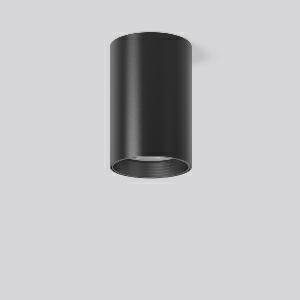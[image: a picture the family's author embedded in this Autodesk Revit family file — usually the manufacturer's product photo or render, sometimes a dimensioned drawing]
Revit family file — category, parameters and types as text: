
# Revit family: heledon_maxi_a_931227_003_76_2eef
name_source: partatom
category: Lighting Fixtures
units: mm (PartAtom-declared; Revit-internal decimal feet)

## family parameters
Cut with Voids When Loaded = No
Host = Face
Light Source = No
Part Type = Normal
Room Calculation Point = No
Round Connector Dimension = Use Diameter
Shared = No

## types (1)
- HELEDON maxi A (1 x LED Modul 930, 3650 lm, 3000)
    Apparent Load = 35 VA
    Approval mark = CE
    CIE Flux Codes = 97 100 100 100 100
    Color Rendering = 90
    Color Temperature = 3000
    Default Elevation = 1800 mm
    Description = Series: HELEDON maxi
Cylindrical surface-mounted downlight. Housing: die-cast aluminium, powder-coated. Internal ceiling frame polycarbonate with bayonet mounting. Black plastic ring and recessed LED to prevent glare from the side. Optical assembly with lens made of plastic (polycarbonate) for the best homogeneous light distribution - can be changed without tools. Best colour rendering index Ra>90. Suitable for Ceiling mounting. Easy installation with a separate ceiling frame with bayonet mounting and plug connection. Driver integrated. Connected via plug-in connector. High quality converter without flickering and stroboscopic effect. The following accessories can be mounted without use of tools: interchangeable lenses, decorative glasses, honeycomb louvre, clear and frosted diffusers, white interchangeable plastic ring. 
Colour: deep black, matt (RAL 9005)
Diameter: 123 mm
Height: 183 mm
Lamp: LED
Socket: without socket
Colour temperature: 3000K
Colour rendering index (CRI): 92
System power: 35 W
Rated luminous flux: 3650 lm
Luminous efficiency: 104 lm/W
Control gear: Converter, dimmable, DALI
Protection class: I
Type of protection: IP 20
    Height = 183 mm
    Lamp = 1 x LED Modul 930
    Lamp Light Flux = 3650 lm
    Lamp count = 1
    Length = 123 mm
    Lifetime = 50000 h
    Luminous efficacy = 104 lm/W
    Manufacturer = RZB
    ModVariant = No
    Model = 931227.003.76
    Mounting Place = Ceiling
    Mounting Type = Surface mounted
    Number of Poles = 1
    OnlyDefault = Yes
    Power Factor = 1
    Product Name = HELEDON maxi A
    Product group = Surface mounted downlights
    ProductGroupID = 302
    Protection Class = Protection class I
    Protection Degree = IP 20
    RLX_Detail_Level = 1
    RLX_Emergency_Light_Flux = 0 lm
    RLX_Emergency_Type = 0
    RLX_Emergency_Type_DB = No
    RlxData = <blob elided: 97585 chars, md5=f50babf7>
    Socket = socket
    Standby Power = 0 W
    System Light Flux = 3650 lm
    System Power = 35 W
    Type Comments = Product without accessories
    Type Image = 931193.003.jpg
    URL = http://relux.com
    VarID = ---
    Voltage = 230 V
    Voltage Range = 220-240 V
    Weight = 0.00 kg
    Width = 0 mm  [stored 0 ft]

note: [stored X ft] marks values corroborated as IEEE doubles in the binary element streams (Revit-internal decimal feet)

## geometry (parser evidence)
native form markers: Blend x4, Sweep x10
no freeform markers — native parametric forms only
